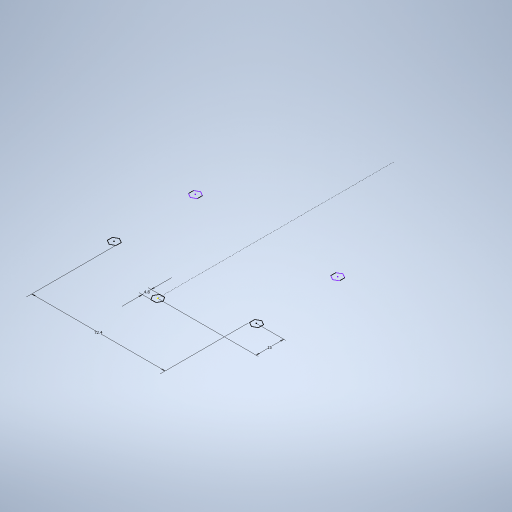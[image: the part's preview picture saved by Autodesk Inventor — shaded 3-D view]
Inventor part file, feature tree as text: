
AUTODESK INVENTOR PART (.ipt)
format: ipt  version: 2024.2 (Build 282272000, 272)  size: 240,640 bytes
history: native  units: mm
features: sketch x1
ambient origin geometry x8: Origin, YZ Plane, XZ Plane, XY Plane, X Axis, Y Axis, Z Axis, Center Point
feature tree (1):
  sketch  "Sketch1"  dims[d0=4.8mm d1=72.4mm d2=15.0mm]
